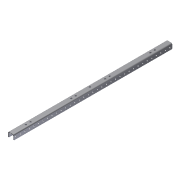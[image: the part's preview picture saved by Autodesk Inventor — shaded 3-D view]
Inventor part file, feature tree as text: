
AUTODESK INVENTOR PART (.ipt)
format: ipt  version: 2011 (Build 150239000, 239)  size: 325,120 bytes
history: native  units: in
note: dims shown in document units (in); Inventor stores cm internally (conversion verified against a paired STEP export)
features: sketch x5, extrude x4, pattern_linear x3, fillet x2, plane x1, mirror x1
ambient origin geometry x8: Origin, YZ Plane, XZ Plane, XY Plane, X Axis, Y Axis, Z Axis, Center Point
bodies: Solid1 (feature_tree)
feature tree (16):
  extrude  "Extrusion1"  Depth=1.25in
  fillet  "Fillet1"  Radius=0.125in
  fillet  "Fillet2"  Radius=0.125in
  extrude  "Extrusion2"  TaperAngle=0.0deg  [1 undecoded]
  pattern_linear  "Rectangular Pattern1"  Spacing1=0.25in  [1 undecoded]
  extrude  "Extrusion3"  Depth=0.5in
  pattern_linear  "Rectangular Pattern2"  Spacing1=0.5in  [1 undecoded]
  pattern_linear  "Rectangular Pattern3"  Spacing1=35.0in  [1 undecoded]
  plane  "Work Plane2"
  mirror  "Mirror1"
  extrude  "Extrusion4"  Depth=13.7795in
  sketch  "Sketch8"  dims[d9=0.125in d10=0.25in d11=0.5in d12=0.5in d13=35.0in d14=0.0in d15=13.7795in d17=1.0in d18=0.375in d20=3.25in d21=35.0in d22=0.0in d23=0.7874in d25=1.0in d26=0.7874in d28=10.0in d30=0.5625in d31=0.375in d32=0.5625in d33=17.5in d34=35.0in d35=0.0in]
  sketch  "Sketch1"  dims[d0=1.0in d1=1.25in d2=0.125in d3=0.125in]
  sketch  "Sketch2"  dims[d4=1.125in d5=0.0in]
  sketch  "Sketch3"  dims[d6=35.0in d7=0.0in]
  sketch  "Sketch5"  dims[d8=0.25in]
note: 4 required parameter values undecoded (feature->parameter linkage not recoverable at this tier; creation-order binding heuristic only, values carry confidence <= 0.55)
